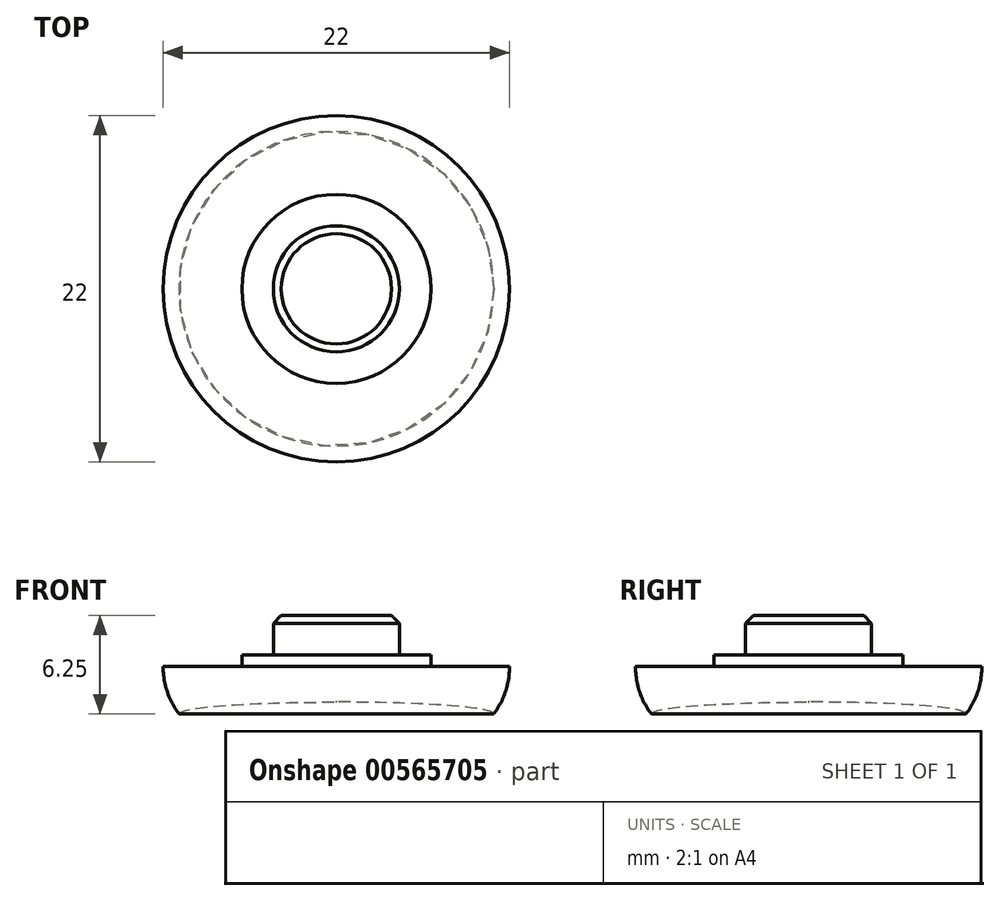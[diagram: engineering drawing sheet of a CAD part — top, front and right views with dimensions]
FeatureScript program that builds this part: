
annotation { "Feature Type Name" : "Feature", "Feature Type Description" : "" }
export const myFeature = defineFeature(function(context is Context, id is Id, definition is map)
    precondition{}
    {
        {
            var Q0;
            Q0=qCreatedBy(makeId("Front.planeOp"),FACE);
            var sketch = newSketch(context, id + "F0", { "sketchPlane" : qUnion([Q0])});
            skLineSegment(sketch, "E0", {"start": v(0, 6.25) * mm, "end": v(4, 6.25) * mm});
            skLineSegment(sketch, "E1", {"start": v(4, 6.25) * mm, "end": v(4, 3.75) * mm});
            skLineSegment(sketch, "E2", {"start": v(4, 3.75) * mm, "end": v(6, 3.75) * mm});
            skLineSegment(sketch, "E3", {"start": v(6, 3.75) * mm, "end": v(6, 3) * mm});
            skLineSegment(sketch, "E4", {"start": v(6, 3) * mm, "end": v(11, 3) * mm});
            skLineSegment(sketch, "E5", {"start": v(11, 3) * mm, "end": v(11, 0) * mm});
            skLineSegment(sketch, "E6", {"start": v(12.47, 0) * mm, "end": v(11, 0) * mm});
            skEllipticalArc(sketch, "E7", {});
            skLineSegment(sketch, "E8", {"start": v(0, 6.25) * mm, "end": v(0, 0.75) * mm});
            skLineSegment(sketch, "E9", {"start": v(11, 0) * mm, "end": v(10, 0) * mm});
            skPoint(sketch, "E10.orphan", {"position": v(0, 6.86) * mm});
            const initialGuessF0  = {"E7": [0, 0, 1, 0, 0.01, 0.00075, 0, 1.5707963267948966]};
            skSetInitialGuess(sketch, initialGuessF0);
            skSolve(sketch);
        }
        {
            var Q0;
            Q0=qSketchRegion(id+"F0",true);
            var Q1;
            Q1=sQuery(id+"F0.wireOp",EDGE,"E8");
            revolve(context, id + "F1", {"entities" : qUnion([Q0]), "axis" : qUnion([Q1]), "revolveType" : RevolveType.FULL});
        }
        {
            var Q0;
            Q0=makeQuery(id+"F1.opRevolve","SWEPT_EDGE",EDGE,{"disambiguationData":[OSD([sQuery(id+"F0.wireOp",EDGE,"E5"),sQuery(id+"F0.wireOp",EDGE,"E9")])]});
            fillet(context, id + "F2", {"entities" : qUnion([Q0]), "radius" : 5 * mm, "tangentPropagation" : true, "allowEdgeOverflow" : false});
        }
        {
            var Q0;
            Q0=makeQuery(id+"F1.opRevolve","SWEPT_EDGE",EDGE,{"disambiguationData":[OSD([sQuery(id+"F0.wireOp",EDGE,"E0"),sQuery(id+"F0.wireOp",EDGE,"E1")])]});
            chamfer(context, id + "F3", {"entities" : qUnion([Q0]), "width" : .5 * mm, "tangentPropagation" : true});
        }
    });
